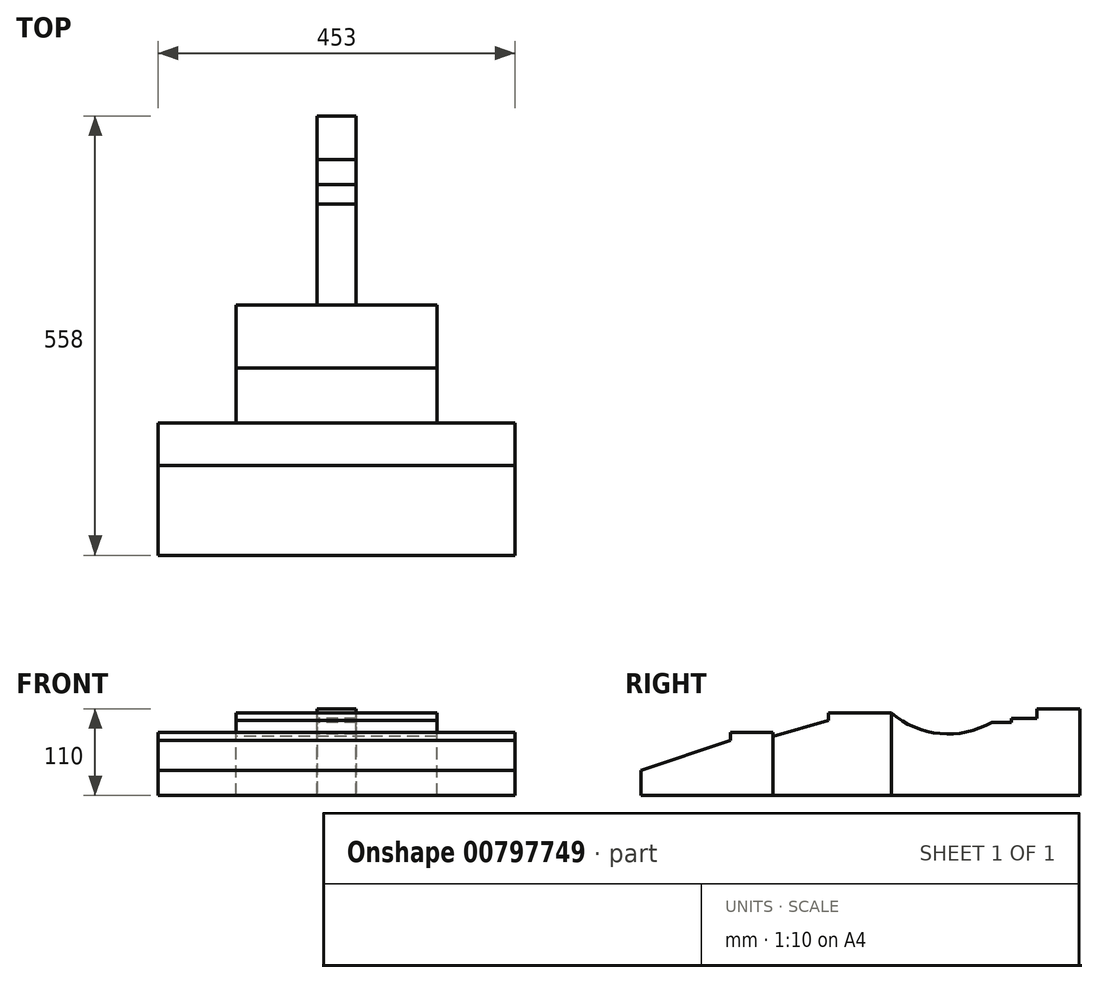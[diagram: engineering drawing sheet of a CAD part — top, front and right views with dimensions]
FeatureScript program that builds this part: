
annotation { "Feature Type Name" : "Feature", "Feature Type Description" : "" }
export const myFeature = defineFeature(function(context is Context, id is Id, definition is map)
    precondition{}
    {
        {
            var Q0;
            Q0=qCreatedBy(makeId("Right.planeOp"),FACE);
            var sketch = newSketch(context, id + "F0", { "sketchPlane" : qUnion([Q0])});
            skLineSegment(sketch, "E0", {"start": v(0, 0) * mm, "end": v(-240, 0) * mm});
            skLineSegment(sketch, "E1", {"start": v(-240, 0) * mm, "end": v(-240, 105) * mm});
            skLineSegment(sketch, "E2", {"start": v(0, 110) * mm, "end": v(0, 0) * mm});
            skLineSegment(sketch, "E3.trimOffspring", {"start": v(-55, 110) * mm, "end": v(0, 110) * mm});
            skLineSegment(sketch, "E4", {"start": v(-55, 110) * mm, "end": v(-55, 98) * mm});
            skLineSegment(sketch, "E5", {"start": v(-55, 98) * mm, "end": v(-87, 98) * mm});
            skLineSegment(sketch, "E6", {"start": v(-87, 98) * mm, "end": v(-87, 93) * mm});
            skLineSegment(sketch, "E7", {"start": v(-87, 93) * mm, "end": v(-112, 93) * mm});
            skArc(sketch, "E8", {"start": v(-240, 105) * mm, "mid": v(-177.92, 78.48) * mm, "end": v(-112, 93) * mm});
            skSolve(sketch);
        }
        {
            var Q0;
            Q0 = qSketchRegion(id + "F0", true);
            extrude(context, id + "F1", {"entities" : qUnion([Q0]), "depth" : 50 * mm, "offsetDistance" : 25 * mm});
        }
        {
            var Q0;
            Q0=makeQuery(id+"F1.opExtrude","SWEPT_FACE",FACE,{"disambiguationData":[OSD([sQuery(id+"F0.wireOp",EDGE,"E1")])]});
            var sketch = newSketch(context, id + "F2", { "sketchPlane" : qUnion([Q0])});
            skLineSegment(sketch, "E9.bottom", {"start": v(-102.5, 0) * mm, "end": v(152.5, 0) * mm});
            skLineSegment(sketch, "E9.top", {"start": v(-102.5, 105) * mm, "end": v(152.5, 105) * mm});
            skLineSegment(sketch, "E9.left", {"start": v(-102.5, 0) * mm, "end": v(-102.5, 105) * mm});
            skLineSegment(sketch, "E9.right", {"start": v(152.5, 0) * mm, "end": v(152.5, 105) * mm});
            skPoint(sketch, "E10.startSnap0", {"position": v(25, 105) * mm});
            skSolve(sketch);
        }
        {
            var Q0;
            Q0 = qSketchRegion(id + "F2", true);
            extrude(context, id + "F3", {"entities" : qUnion([Q0]), "depth" : 150 * mm, "offsetDistance" : 25 * mm});
        }
        {
            var Q0;
            Q0=qCreatedBy(makeId("Right.planeOp"),FACE);
            var sketch = newSketch(context, id + "F4", { "sketchPlane" : qUnion([Q0])});
            skLineSegment(sketch, "E11.bottom", {"start": v(-390, 105) * mm, "end": v(-320, 105) * mm});
            skLineSegment(sketch, "E11.left", {"start": v(-390, 105) * mm, "end": v(-390, 75) * mm});
            skLineSegment(sketch, "E11.right", {"start": v(-320, 105) * mm, "end": v(-320, 95) * mm});
            skLineSegment(sketch, "E12", {"start": v(-320, 95) * mm, "end": v(-390, 75) * mm});
            skSolve(sketch);
        }
        {
            var Q0;
            Q0 = qSketchRegion(id + "F4", true);
            extrude(context, id + "F5", {"entities" : qUnion([Q0]), "operationType" : NewBodyOperationType.REMOVE, "endBound" : BoundingType.UP_TO_NEXT, "depth" : 25 * mm, "offsetDistance" : 25 * mm, "hasSecondDirection" : true, "secondDirectionBound" : SecondDirectionBoundingType.UP_TO_NEXT, "secondDirectionOppositeDirection" : true, "secondDirectionDepth" : 25 * mm});
        }
        {
            var Q0;
            Q0=makeQuery(id+"F3.opExtrude","CAP_FACE",FACE,{"disambiguationData":[OSD([sQuery(id+"F2.wireOp",EDGE,"E9.bottom"),sQuery(id+"F2.wireOp",EDGE,"E9.top"),sQuery(id+"F2.wireOp",EDGE,"E9.left"),sQuery(id+"F2.wireOp",EDGE,"E9.right")])],"isStart":false});
            var sketch = newSketch(context, id + "F6", { "sketchPlane" : qUnion([Q0])});
            skLineSegment(sketch, "E13.bottom", {"start": v(-201.5, 80) * mm, "end": v(251.5, 80) * mm});
            skLineSegment(sketch, "E13.top", {"start": v(-201.5, 0) * mm, "end": v(251.5, 0) * mm});
            skLineSegment(sketch, "E13.left", {"start": v(-201.5, 80) * mm, "end": v(-201.5, 0) * mm});
            skLineSegment(sketch, "E13.right", {"start": v(251.5, 80) * mm, "end": v(251.5, 0) * mm});
            skSolve(sketch);
        }
        {
            var Q0;
            Q0 = qSketchRegion(id + "F6", true);
            extrude(context, id + "F7", {"entities" : qUnion([Q0]), "depth" : 168 * mm, "offsetDistance" : 25 * mm});
        }
        {
            var Q0;
            Q0=qCreatedBy(makeId("Right.planeOp"),FACE);
            var sketch = newSketch(context, id + "F8", { "sketchPlane" : qUnion([Q0])});
            skLineSegment(sketch, "E14.bottom", {"start": v(-558, 80) * mm, "end": v(-444, 80) * mm});
            skLineSegment(sketch, "E14.left", {"start": v(-558, 80) * mm, "end": v(-558, 32) * mm});
            skLineSegment(sketch, "E14.right", {"start": v(-444, 80) * mm, "end": v(-444, 70) * mm});
            skLineSegment(sketch, "E15", {"start": v(-444, 70) * mm, "end": v(-558, 32) * mm});
            skSolve(sketch);
        }
        {
            var Q0;
            Q0 = qSketchRegion(id + "F8", true);
            extrude(context, id + "F9", {"entities" : qUnion([Q0]), "operationType" : NewBodyOperationType.REMOVE, "endBound" : BoundingType.UP_TO_NEXT, "oppositeDirection" : true, "depth" : 25 * mm, "offsetDistance" : 25 * mm, "hasSecondDirection" : true, "secondDirectionBound" : SecondDirectionBoundingType.UP_TO_NEXT, "secondDirectionOppositeDirection" : false, "secondDirectionDepth" : 25 * mm});
        }
    });
